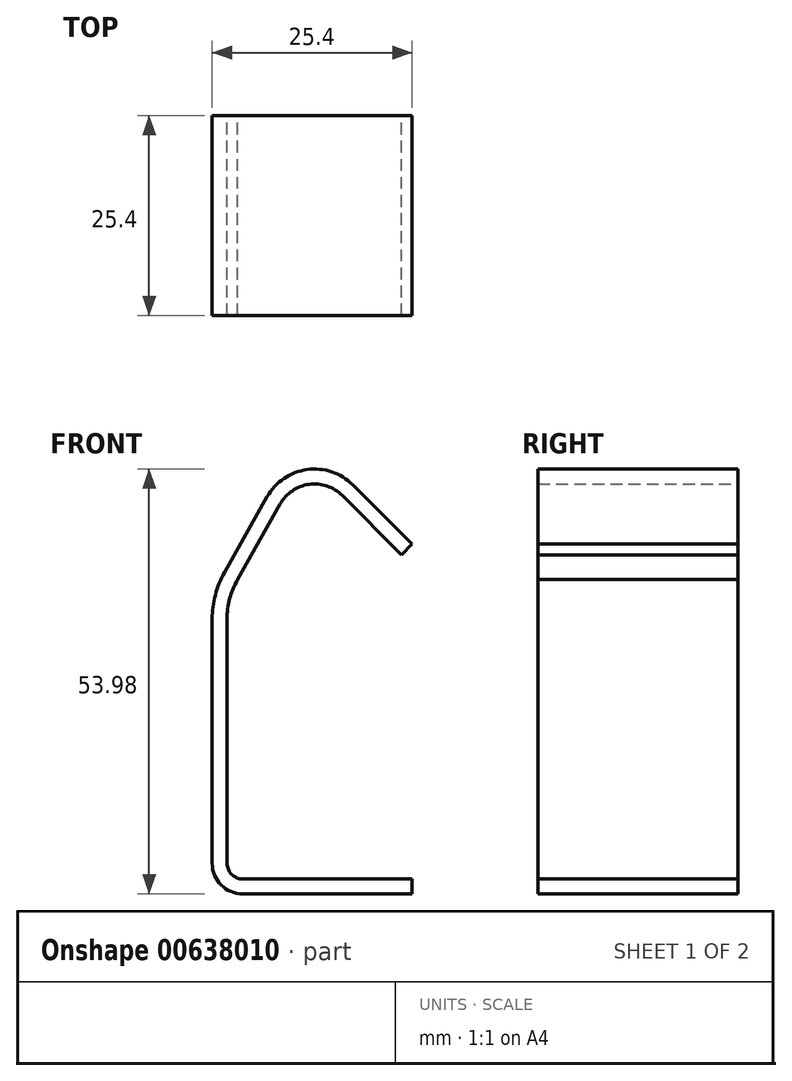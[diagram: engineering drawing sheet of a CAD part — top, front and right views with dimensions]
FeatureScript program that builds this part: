
annotation { "Feature Type Name" : "Feature", "Feature Type Description" : "" }
export const myFeature = defineFeature(function(context is Context, id is Id, definition is map)
    precondition{}
    {
        {
            var Q0;
            Q0=qCreatedBy(makeId("Front.planeOp"),FACE);
            var sketch = newSketch(context, id + "F0", { "sketchPlane" : qUnion([Q0])});
            skLineSegment(sketch, "E0", {"start": v(25.4, 0) * mm, "end": v(3.9, 0) * mm});
            skLineSegment(sketch, "E1", {"start": v(0, 3.9) * mm, "end": v(0, 34.93) * mm});
            skPoint(sketch, "E2.visualSharp", {"position": v(0, 37.6) * mm});
            skPoint(sketch, "E3.visualSharp", {"position": v(11.27, 57.12) * mm});
            skLineSegment(sketch, "E4.0", {"start": v(16.53, 50.61) * mm, "end": v(24.06, 43.09) * mm});
            skLineSegment(sketch, "E4.1", {"start": v(25.4, 1.9) * mm, "end": v(3.9, 1.9) * mm});
            skLineSegment(sketch, "E4.2", {"start": v(1.9, 3.9) * mm, "end": v(1.9, 34.93) * mm});
            skArc(sketch, "E4.3", {"start": v(3.23, 39.92) * mm, "mid": v(2.24, 37.5) * mm, "end": v(1.9, 34.93) * mm});
            skLineSegment(sketch, "E4.4", {"start": v(3.23, 39.92) * mm, "end": v(8.64, 49.53) * mm});
            skPoint(sketch, "E5.visualSharp", {"position": v(11.87, 55.27) * mm});
            skArc(sketch, "E5.filletArc", {"start": v(16.53, 50.61) * mm, "mid": v(12.32, 52.03) * mm, "end": v(8.64, 49.53) * mm});
            skArc(sketch, "E6.0", {"start": v(1.58, 40.86) * mm, "mid": v(0.4, 38) * mm, "end": v(0, 34.92) * mm});
            skLineSegment(sketch, "E6.1", {"start": v(1.58, 40.86) * mm, "end": v(6.99, 50.46) * mm});
            skArc(sketch, "E6.2", {"start": v(17.88, 51.95) * mm, "mid": v(12.06, 53.91) * mm, "end": v(6.99, 50.46) * mm});
            skLineSegment(sketch, "E6.3", {"start": v(17.88, 51.95) * mm, "end": v(25.4, 44.43) * mm});
            skLineSegment(sketch, "E7", {"start": v(25.4, 44.43) * mm, "end": v(24.06, 43.09) * mm});
            skPoint(sketch, "E8.visualSharp", {"position": v(1.9, 1.9) * mm});
            skArc(sketch, "E8.filletArc", {"start": v(1.9, 3.9) * mm, "mid": v(2.48, 2.48) * mm, "end": v(3.9, 1.9) * mm});
            skArc(sketch, "E9.0", {"start": v(0, 3.9) * mm, "mid": v(1.14, 1.14) * mm, "end": v(3.9, 0) * mm});
            skLineSegment(sketch, "E10", {"start": v(25.4, 1.9) * mm, "end": v(25.4, 0) * mm});
            skSolve(sketch);
        }
        {
            var Q0;
            Q0 = qSketchRegion(id + "F0", true);
            extrude(context, id + "F1", {"entities" : qUnion([Q0]), "depth" : 25.4 * mm, "offsetDistance" : 25.4 * mm});
        }
    });
